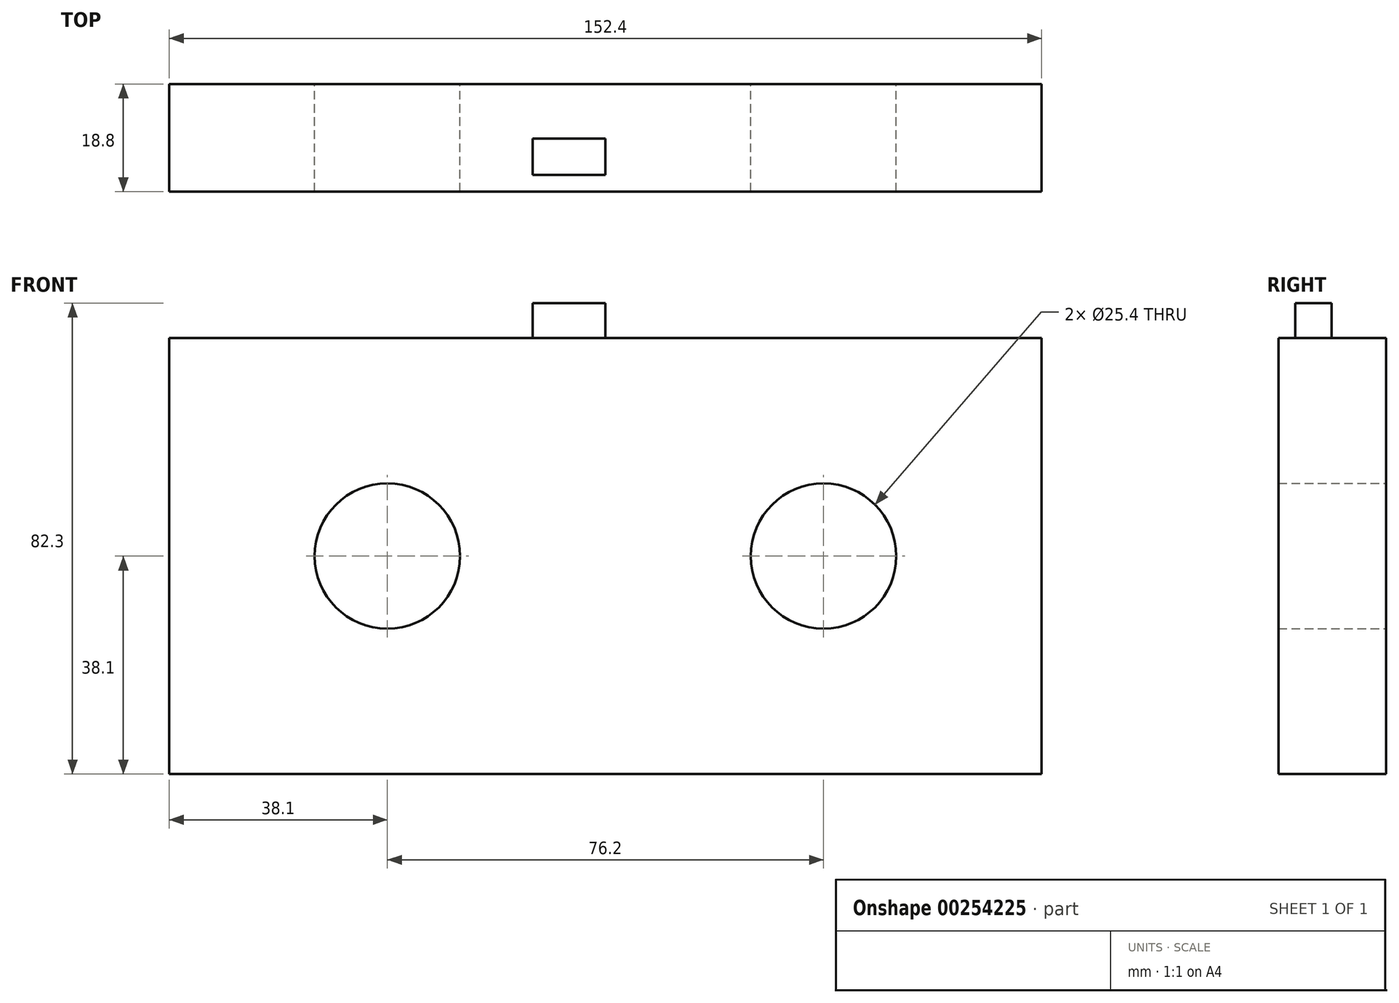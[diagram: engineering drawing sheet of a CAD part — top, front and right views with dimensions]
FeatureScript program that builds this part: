
annotation { "Feature Type Name" : "Feature", "Feature Type Description" : "" }
export const myFeature = defineFeature(function(context is Context, id is Id, definition is map)
    precondition{}
    {
        {
            var Q0;
            Q0=qCreatedBy(makeId("Front.planeOp"),FACE);
            var sketch = newSketch(context, id + "F0", { "sketchPlane" : qUnion([Q0])});
            skLineSegment(sketch, "E0.bottom", {"start": v(76.2, -38.1) * mm, "end": v(-76.2, -38.1) * mm});
            skLineSegment(sketch, "E0.top", {"start": v(76.2, 38.1) * mm, "end": v(-76.2, 38.1) * mm});
            skLineSegment(sketch, "E0.left", {"start": v(76.2, -38.1) * mm, "end": v(76.2, 38.1) * mm});
            skLineSegment(sketch, "E0.right", {"start": v(-76.2, -38.1) * mm, "end": v(-76.2, 38.1) * mm});
            skPoint(sketch, "E0.middle", {"position": v(0, 0) * mm});
            skCircle(sketch, "E1", {"center": v(-38.1, 0) * mm, "radius": 12.7 * mm});
            skLineSegment(sketch, "E2.bottom", {"start": v(76.2, -38.1) * mm, "end": v(0, -38.1) * mm});
            skLineSegment(sketch, "E2.top", {"start": v(76.2, 38.1) * mm, "end": v(0, 38.1) * mm});
            skLineSegment(sketch, "E2.right", {"start": v(0, -38.1) * mm, "end": v(0, 38.1) * mm});
            skPoint(sketch, "E2.middle", {"position": v(76.2, 0) * mm});
            skCircle(sketch, "E3", {"center": v(38.1, 0) * mm, "radius": 12.7 * mm});
            skPoint(sketch, "E2.left.end.orphan", {"position": v(152.4, 38.1) * mm});
            skPoint(sketch, "E2.left.start.orphan", {"position": v(152.4, -38.1) * mm});
            skSolve(sketch);
        }
        {
            var Q0;
            Q0=qCreatedBy(makeId("Top.planeOp"),FACE);
            var sketch = newSketch(context, id + "F1", { "sketchPlane" : qUnion([Q0])});
            skLineSegment(sketch, "E4.bottom", {"start": v(0, -9.53) * mm, "end": v(-12.7, -9.53) * mm});
            skLineSegment(sketch, "E4.top", {"start": v(0, -15.88) * mm, "end": v(-12.7, -15.88) * mm});
            skLineSegment(sketch, "E4.left", {"start": v(0, -9.53) * mm, "end": v(0, -15.88) * mm});
            skLineSegment(sketch, "E4.right", {"start": v(-12.7, -9.53) * mm, "end": v(-12.7, -15.88) * mm});
            skSolve(sketch);
        }
        {
            var Q0;
            Q0 = qSketchRegion(id + "F0", true);
            extrude(context, id + "F2", {"entities" : qUnion([Q0]), "depth" : 18.8 * mm});
        }
        {
            var Q0;
            Q0 = qSketchRegion(id + "F1", true);
            extrude(context, id + "F3", {"entities" : qUnion([Q0]), "operationType" : NewBodyOperationType.ADD, "depth" : 44.2 * mm});
        }
    });
